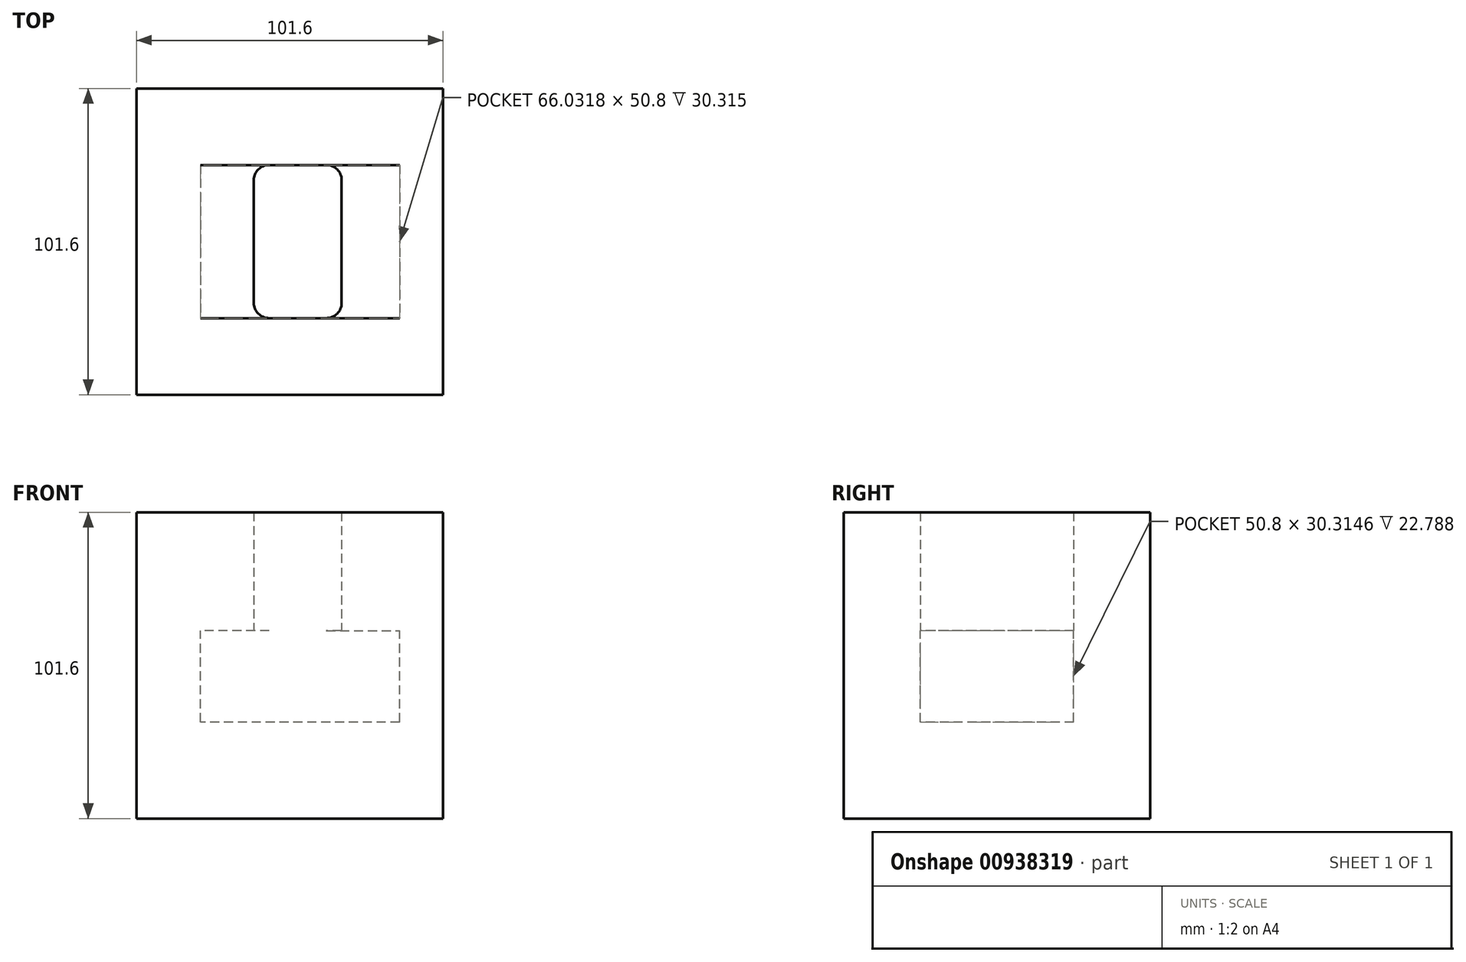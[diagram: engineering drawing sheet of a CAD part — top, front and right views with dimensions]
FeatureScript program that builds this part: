
annotation { "Feature Type Name" : "Feature", "Feature Type Description" : "" }
export const myFeature = defineFeature(function(context is Context, id is Id, definition is map)
    precondition{}
    {
        {
            var Q0;
            Q0=qCreatedBy(makeId("Front.planeOp"),FACE);
            var sketch = newSketch(context, id + "F0", { "sketchPlane" : qUnion([Q0])});
            skLineSegment(sketch, "E0.bottom", {"start": v(0, 0) * mm, "end": v(101.6, 0) * mm});
            skLineSegment(sketch, "E0.top", {"start": v(0, 101.6) * mm, "end": v(101.6, 101.6) * mm});
            skLineSegment(sketch, "E0.left", {"start": v(0, 0) * mm, "end": v(0, 101.6) * mm});
            skLineSegment(sketch, "E0.right", {"start": v(101.6, 0) * mm, "end": v(101.6, 101.6) * mm});
            skSolve(sketch);
        }
        {
            var Q0;
            Q0 = qSketchRegion(id + "F0", true);
            extrude(context, id + "F1", {"entities" : qUnion([Q0]), "depth" : 50.8 * mm, "offsetDistance" : 25.4 * mm});
        }
        {
            var Q0;
            Q0=makeQuery(id+"F1.opExtrude","CAP_FACE",FACE,{"disambiguationData":[OSD([sQuery(id+"F0.wireOp",EDGE,"E0.bottom"),sQuery(id+"F0.wireOp",EDGE,"E0.top"),sQuery(id+"F0.wireOp",EDGE,"E0.left"),sQuery(id+"F0.wireOp",EDGE,"E0.right")])],"isStart":false});
            var sketch = newSketch(context, id + "F2", { "sketchPlane" : qUnion([Q0])});
            skLineSegment(sketch, "E1.bottom", {"start": v(38.89, 101.6) * mm, "end": v(68, 101.6) * mm});
            skLineSegment(sketch, "E1.top", {"start": v(38.89, 31.98) * mm, "end": v(68, 31.98) * mm});
            skLineSegment(sketch, "E1.left", {"start": v(38.89, 101.6) * mm, "end": v(38.89, 31.98) * mm});
            skLineSegment(sketch, "E1.right", {"start": v(68, 101.6) * mm, "end": v(68, 31.98) * mm});
            skLineSegment(sketch, "E2.bottom", {"start": v(68, 31.98) * mm, "end": v(87.21, 31.98) * mm});
            skLineSegment(sketch, "E2.top", {"start": v(68, 62.3) * mm, "end": v(87.21, 62.3) * mm});
            skLineSegment(sketch, "E2.left", {"start": v(68, 31.98) * mm, "end": v(68, 62.3) * mm});
            skLineSegment(sketch, "E2.right", {"start": v(87.21, 31.98) * mm, "end": v(87.21, 62.3) * mm});
            skLineSegment(sketch, "E3.bottom", {"start": v(38.89, 31.98) * mm, "end": v(21.18, 31.98) * mm});
            skLineSegment(sketch, "E3.top", {"start": v(38.89, 62.3) * mm, "end": v(21.18, 62.3) * mm});
            skLineSegment(sketch, "E3.left", {"start": v(38.89, 31.98) * mm, "end": v(38.89, 62.3) * mm});
            skLineSegment(sketch, "E3.right", {"start": v(21.18, 31.98) * mm, "end": v(21.18, 62.3) * mm});
            skSolve(sketch);
        }
        {
            var Q0;
            Q0 = qSketchRegion(id + "F2", true);
            extrude(context, id + "F3", {"entities" : qUnion([Q0]), "operationType" : NewBodyOperationType.REMOVE, "oppositeDirection" : true, "depth" : 25.4 * mm, "offsetDistance" : 25.4 * mm});
        }
        {
            var Q0;
            Q0=makeQuery(id+"F1.opExtrude","SWEPT_BODY",BODY,{"disambiguationData":[OSD([sQuery(id+"F0.wireOp",EDGE,"E0.bottom"),sQuery(id+"F0.wireOp",EDGE,"E0.top"),sQuery(id+"F0.wireOp",EDGE,"E0.left"),sQuery(id+"F0.wireOp",EDGE,"E0.right")])]});
            var Q1;
            Q1=makeQuery(id+"F1.opExtrude","CAP_FACE",FACE,{"disambiguationData":[OSD([sQuery(id+"F0.wireOp",EDGE,"E0.bottom"),sQuery(id+"F0.wireOp",EDGE,"E0.top"),sQuery(id+"F0.wireOp",EDGE,"E0.left"),sQuery(id+"F0.wireOp",EDGE,"E0.right")])],"isStart":false});
            mirror(context, id + "F4", {"operationType" : NewBodyOperationType.ADD, "entities" : qUnion([Q0]), "mirrorPlane" : qUnion([Q1])});
        }
        {
            var Q0;
            Q0=makeQuery(id+"F3.boolean.opBoolean","COPY",EDGE,{"derivedFrom":makeQuery(id+"F3.opExtrude","CAP_EDGE",EDGE,{"disambiguationData":[OSD([sQuery(id+"F2.wireOp",EDGE,"E1.right")])],"isStart":false})});
            var Q1;
            Q1=makeQuery(id+"F3.boolean.opBoolean","COPY",EDGE,{"derivedFrom":makeQuery(id+"F3.opExtrude","CAP_EDGE",EDGE,{"disambiguationData":[OSD([sQuery(id+"F2.wireOp",EDGE,"E1.left")])],"isStart":false})});
            var Q2;
            Q2=makeQuery(id+"F4.opPattern","COPY",EDGE,{"derivedFrom":makeQuery(id+"F3.boolean.opBoolean","COPY",EDGE,{"derivedFrom":makeQuery(id+"F3.opExtrude","CAP_EDGE",EDGE,{"disambiguationData":[OSD([sQuery(id+"F2.wireOp",EDGE,"E1.right")])],"isStart":false})}),"instanceName":"1"});
            var Q3;
            Q3=makeQuery(id+"F4.opPattern","COPY",EDGE,{"derivedFrom":makeQuery(id+"F3.boolean.opBoolean","COPY",EDGE,{"derivedFrom":makeQuery(id+"F3.opExtrude","CAP_EDGE",EDGE,{"disambiguationData":[OSD([sQuery(id+"F2.wireOp",EDGE,"E1.left")])],"isStart":false})}),"instanceName":"1"});
            fillet(context, id + "F5", {"entities" : qUnion([Q0, Q1, Q2, Q3]), "radius" : 5.08 * mm, "tangentPropagation" : true, "allowEdgeOverflow" : false});
        }
    });
